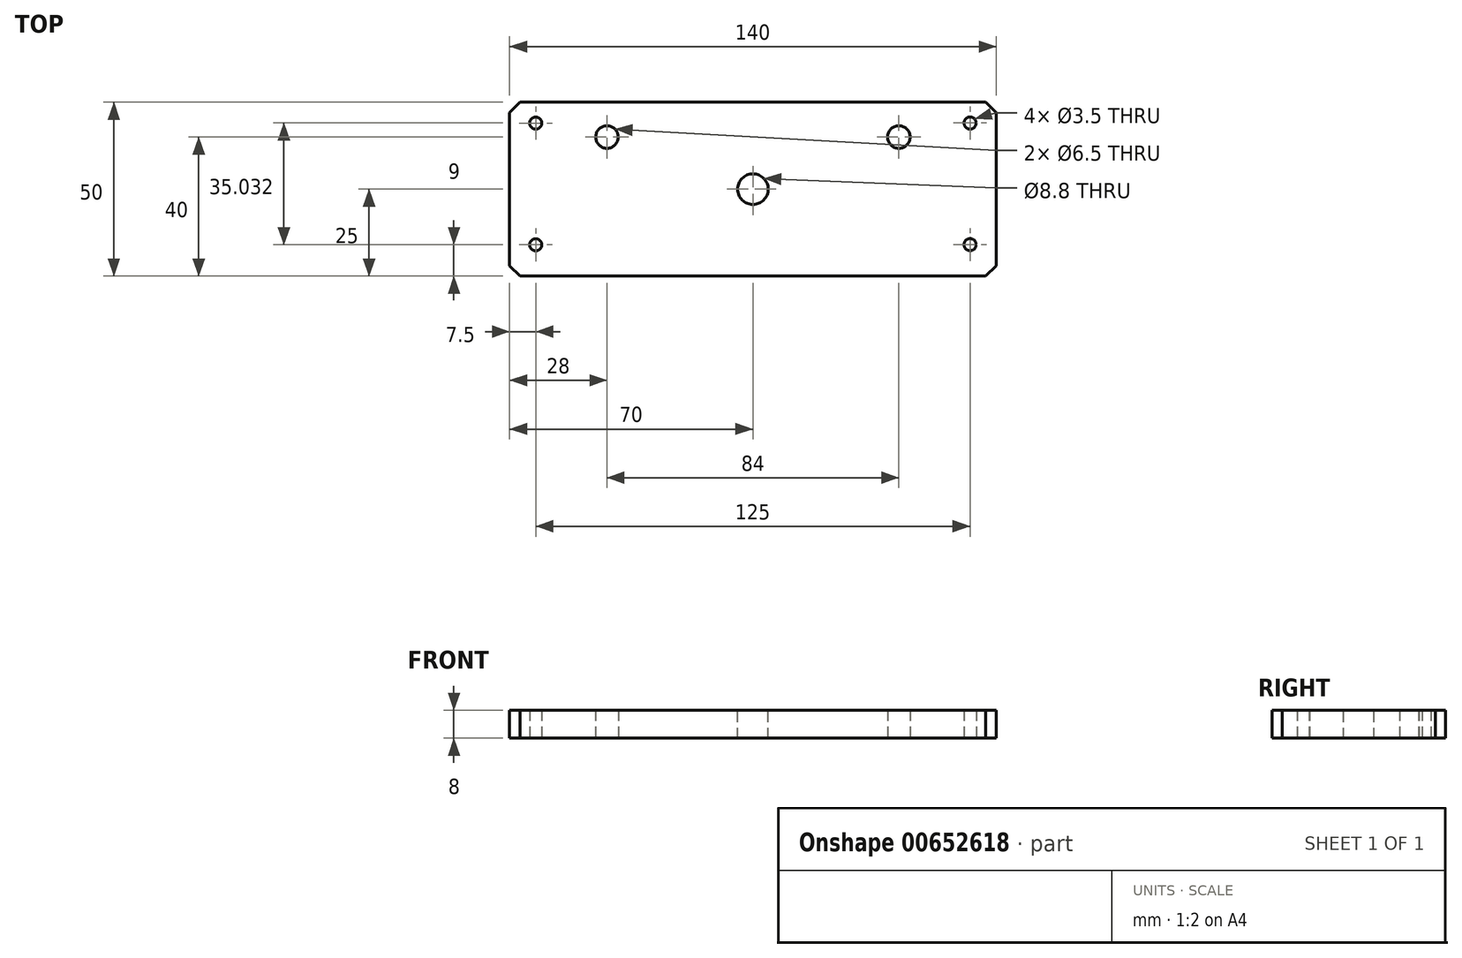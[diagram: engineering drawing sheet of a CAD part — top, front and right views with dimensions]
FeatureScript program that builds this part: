
annotation { "Feature Type Name" : "Feature", "Feature Type Description" : "" }
export const myFeature = defineFeature(function(context is Context, id is Id, definition is map)
    precondition{}
    {
        {
            var Q0;
            Q0=qCreatedBy(makeId("Top.planeOp"),FACE);
            var sketch = newSketch(context, id + "F0", { "sketchPlane" : qUnion([Q0])});
            skLineSegment(sketch, "E0.bottom", {"start": v(-70, 25) * mm, "end": v(70, 25) * mm});
            skLineSegment(sketch, "E0.top", {"start": v(-70, -25) * mm, "end": v(70, -25) * mm});
            skLineSegment(sketch, "E0.left", {"start": v(-70, 25) * mm, "end": v(-70, -25) * mm});
            skLineSegment(sketch, "E0.right", {"start": v(70, 25) * mm, "end": v(70, -25) * mm});
            skCircle(sketch, "E1", {"center": v(62.5, 19.03) * mm, "radius": 1.75 * mm});
            skLineSegment(sketch, "E2", {"start": v(62.5, 19.03) * mm, "end": v(-63.34, 19.03) * mm, "construction": true});
            skLineSegment(sketch, "E3", {"start": v(62.5, 19.03) * mm, "end": v(62.5, -20.81) * mm, "construction": true});
            skCircle(sketch, "E4.0.1.0", {"center": v(62.5, -15.97) * mm, "radius": 1.75 * mm});
            skCircle(sketch, "E4.1.0.0", {"center": v(-62.5, 19) * mm, "radius": 1.75 * mm});
            skCircle(sketch, "E4.1.1.0", {"center": v(-62.5, -16) * mm, "radius": 1.75 * mm});
            skLineSegment(sketch, "E4.direction1", {"start": v(62.5, 19.03) * mm, "end": v(-62.5, 19) * mm, "construction": true});
            skLineSegment(sketch, "E4.direction2", {"start": v(62.5, 19.03) * mm, "end": v(62.5, -15.97) * mm, "construction": true});
            skCircle(sketch, "E5", {"center": v(42, 15) * mm, "radius": 3.25 * mm});
            skCircle(sketch, "E6.MirrorC", {"center": v(-42, 15) * mm, "radius": 3.25 * mm});
            skCircle(sketch, "E7", {"center": v(0, 0) * mm, "radius": 2.5 * mm});
            skSolve(sketch);
        }
        {
            var Q0;
            Q0 = qSketchRegion(id + "F0", true);
            extrude(context, id + "F1", {"entities" : qUnion([Q0]), "depth" : 8 * mm, "offsetDistance" : 25 * mm});
        }
        {
            var Q0;
            Q0=makeQuery(id+"F1.opExtrude","SWEPT_EDGE",EDGE,{"disambiguationData":[OSD([sQuery(id+"F0.wireOp",EDGE,"E0.top"),sQuery(id+"F0.wireOp",EDGE,"E0.left")])]});
            var Q1;
            Q1=makeQuery(id+"F1.opExtrude","SWEPT_EDGE",EDGE,{"disambiguationData":[OSD([sQuery(id+"F0.wireOp",EDGE,"E0.top"),sQuery(id+"F0.wireOp",EDGE,"E0.right")])]});
            var Q2;
            Q2=makeQuery(id+"F1.opExtrude","SWEPT_EDGE",EDGE,{"disambiguationData":[OSD([sQuery(id+"F0.wireOp",EDGE,"E0.bottom"),sQuery(id+"F0.wireOp",EDGE,"E0.right")])]});
            var Q3;
            Q3=makeQuery(id+"F1.opExtrude","SWEPT_EDGE",EDGE,{"disambiguationData":[OSD([sQuery(id+"F0.wireOp",EDGE,"E0.bottom"),sQuery(id+"F0.wireOp",EDGE,"E0.left")])]});
            chamfer(context, id + "F2", {"entities" : qUnion([Q0, Q1, Q2, Q3]), "width" : 3 * mm, "tangentPropagation" : true});
        }
        {
            var Q0;
            Q0=makeQuery(id+"F1.opExtrude","CAP_FACE",FACE,{"disambiguationData":[OSD([sQuery(id+"F0.wireOp",EDGE,"E0.bottom"),sQuery(id+"F0.wireOp",EDGE,"E0.top"),sQuery(id+"F0.wireOp",EDGE,"E0.left"),sQuery(id+"F0.wireOp",EDGE,"E0.right"),sQuery(id+"F0.wireOp",EDGE,"E1"),sQuery(id+"F0.wireOp",EDGE,"E4.0.1.0"),sQuery(id+"F0.wireOp",EDGE,"E4.1.0.0"),sQuery(id+"F0.wireOp",EDGE,"E4.1.1.0"),sQuery(id+"F0.wireOp",EDGE,"E5"),sQuery(id+"F0.wireOp",EDGE,"E6.MirrorC"),sQuery(id+"F0.wireOp",EDGE,"E7")])],"isStart":false});
            var sketch = newSketch(context, id + "F3", { "sketchPlane" : qUnion([Q0])});
            skCircle(sketch, "E8", {"center": v(0, 0) * mm, "radius": 5 * mm});
            skSolve(sketch);
        }
        {
            var Q0;
            Q0=sQuery(id+"F3.wireOp",VERTEX,"E8.center");
            var Q1;
            Q1=makeQuery(id+"F1.opExtrude","SWEPT_BODY",BODY,{"disambiguationData":[OSD([sQuery(id+"F0.wireOp",EDGE,"E0.bottom"),sQuery(id+"F0.wireOp",EDGE,"E0.top"),sQuery(id+"F0.wireOp",EDGE,"E0.left"),sQuery(id+"F0.wireOp",EDGE,"E0.right"),sQuery(id+"F0.wireOp",EDGE,"E1"),sQuery(id+"F0.wireOp",EDGE,"E4.0.1.0"),sQuery(id+"F0.wireOp",EDGE,"E4.1.0.0"),sQuery(id+"F0.wireOp",EDGE,"E4.1.1.0"),sQuery(id+"F0.wireOp",EDGE,"E5"),sQuery(id+"F0.wireOp",EDGE,"E6.MirrorC"),sQuery(id+"F0.wireOp",EDGE,"E7")])]});
            hole(context, id + "F4", {"style" : HoleStyle.SIMPLE, "endStyle" : HoleEndStyle.THROUGH, "standardTappedOrClearance" : lookupTablePath({ "standard" : "ISO", "engagement" : "75%", "pitch" : "1.25 mm", "size" : "M10", "type" : "Tapped" }), "standardBlindInLast" : lookupTablePath({ "standard" : "ISO", "engagement" : "75%", "pitch" : "1.25 mm", "size" : "M10", "type" : "Tapped" }), "holeDiameter" : 8.8 * mm, "majorDiameter" : 10 * mm, "showTappedDepth" : true, "isTappedThrough" : true, "tappedDepth" : 12 * mm, "tapClearance" : 3, "locations" : qUnion([Q0]), "scope" : qUnion([Q1])});
        }
    });
